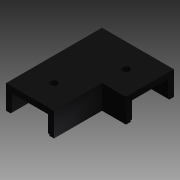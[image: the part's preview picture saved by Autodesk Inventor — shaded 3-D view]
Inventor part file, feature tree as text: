
AUTODESK INVENTOR PART (.ipt)
format: ipt  version: 2014 (Build 180170000, 170)  size: 146,944 bytes
history: native  units: in
note: dims shown in document units (in); Inventor stores cm internally (conversion verified against a paired STEP export)
features: extrude x5, sketch x5, other x2, split x1
ambient origin geometry x8: Origin, YZ Plane, XZ Plane, XY Plane, X Axis, Y Axis, Z Axis, Center Point
bodies: Solid1 (feature_tree)
feature tree (13):
  extrude  "Extrusion1"  Depth=1.0in
  extrude  "Extrusion2"  Depth=0.5in TaperAngle=0.0deg
  extrude  "Extrusion4"  Depth=0.75in
  extrude  "Extrusion5"  Depth=0.75in
  extrude  "Extrusion6"  Depth=0.03in TaperAngle=0.0deg
  split  "Split2"
  other  "Lip4"
  other  "Lip5"
  sketch  "Sketch1"  dims[d0=1.0in d1=1.0in]
  sketch  "Sketch2"  dims[d2=2.0in d3=0.0in d4=0.5in d5=0.0in]
  sketch  "Sketch5"  dims[d8=0.75in d9=0.75in]
  sketch  "Sketch6"  dims[d10=1.75in d11=0.0in d12=0.75in]
  sketch  "Sketch7"  dims[d13=0.75in d14=1.75in d15=0.0in d34=0.141in d35=1.0in d36=0.0in d38=0.03in d39=0.03in d40=0.0in d41=0.0in d42=0.0in d43=0.0in d44=0.03in d45=0.03in d46=0.0in d47=0.0in d48=0.0in d49=0.0in]
